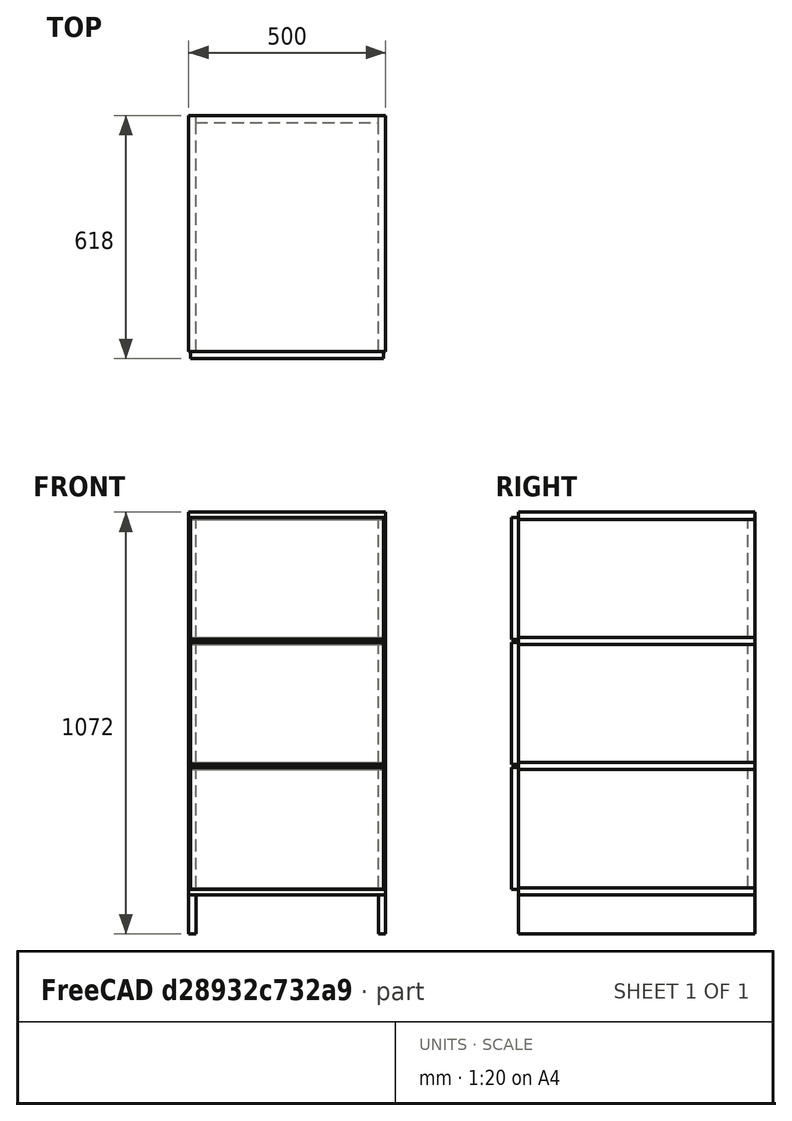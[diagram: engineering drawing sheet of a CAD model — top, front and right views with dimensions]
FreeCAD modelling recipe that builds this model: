
FCSTD DOCUMENT  (FreeCAD 0.20R29177 (Git))
Label: Demo009_approximation
License: All rights reserved
LicenseURL: http://en.wikipedia.org/wiki/All_rights_reserved
objects: Part::Box×18, App::DocumentObjectGroup×10, Spreadsheet::Sheet×1, TechDraw::DrawSVGTemplate×1, TechDraw::DrawViewSpreadsheet×1, TechDraw::DrawPage×1
note: 18 computed .brp shape members not serialized (recipe doc carries the construction recipe); baked Part::Feature solids carry a one-line shape summary decoded from their .brp

FEATURE [Part::Box] Box006  label="Foot L"
  AttacherType = Attacher::AttachEngine3D
  Height = 100
  Length = 18
  Width = 600
FEATURE [Part::Box] Box007  label="Side L1"
  AttacherType = Attacher::AttachEngine3D
  Height = 300
  Length = 18
  Placement = pos=(0,0,118) rot=(0,0,1;0rad)
  Width = 600
FEATURE [Part::Box] Box008  label="Side L2"
  AttacherType = Attacher::AttachEngine3D
  Height = 300
  Length = 18
  Placement = pos=(0,0,436) rot=(0,0,1;0rad)
  Width = 600
FEATURE [Part::Box] Box009  label="Side L3"
  AttacherType = Attacher::AttachEngine3D
  Height = 300
  Length = 18
  Placement = pos=(0,0,754) rot=(0,0,1;0rad)
  Width = 600
FEATURE [Part::Box] Box010  label="Foot R"
  AttacherType = Attacher::AttachEngine3D
  Height = 100
  Length = 18
  Placement = pos=(482,0,0) rot=(0,0,1;0rad)
  Width = 600
FEATURE [Part::Box] Box011  label="Side R1"
  AttacherType = Attacher::AttachEngine3D
  Height = 300
  Length = 18
  Placement = pos=(482,0,118) rot=(0,0,1;0rad)
  Width = 600
FEATURE [Part::Box] Box012  label="Side R2"
  AttacherType = Attacher::AttachEngine3D
  Height = 300
  Length = 18
  Placement = pos=(482,0,436) rot=(0,0,1;0rad)
  Width = 600
FEATURE [Part::Box] Box013  label="Side R3"
  AttacherType = Attacher::AttachEngine3D
  Height = 300
  Length = 18
  Placement = pos=(482,0,754) rot=(0,0,1;0rad)
  Width = 600
FEATURE [Part::Box] Box018  label="Back 1"
  AttacherType = Attacher::AttachEngine3D
  Height = 300
  Length = 464
  Placement = pos=(18,582,118) rot=(0,0,1;0rad)
  Width = 18
FEATURE [Part::Box] Box019  label="Back 2"
  AttacherType = Attacher::AttachEngine3D
  Height = 300
  Length = 464
  Placement = pos=(18,582,436) rot=(0,0,1;0rad)
  Width = 18
FEATURE [Part::Box] Box020  label="Back 3"
  AttacherType = Attacher::AttachEngine3D
  Height = 300
  Length = 464
  Placement = pos=(18,582,754) rot=(0,0,1;0rad)
  Width = 18
FEATURE [Part::Box] Box023  label="Top 1"
  AttacherType = Attacher::AttachEngine3D
  Height = 18
  Length = 500
  Placement = pos=(0,0,100) rot=(0,0,1;0rad)
  Width = 600
FEATURE [Part::Box] Box024  label="Top 2"
  AttacherType = Attacher::AttachEngine3D
  Height = 18
  Length = 500
  Placement = pos=(0,0,418) rot=(0,0,1;0rad)
  Width = 600
FEATURE [Part::Box] Box025  label="Top 3"
  AttacherType = Attacher::AttachEngine3D
  Height = 18
  Length = 500
  Placement = pos=(0,0,736) rot=(0,0,1;0rad)
  Width = 600
FEATURE [Part::Box] Box026  label="Top 4"
  AttacherType = Attacher::AttachEngine3D
  Height = 18
  Length = 500
  Placement = pos=(0,0,1054) rot=(0,0,1;0rad)
  Width = 600
FEATURE [Part::Box] Box027  label="Front 1"
  AttacherType = Attacher::AttachEngine3D
  Height = 310
  Length = 490
  Placement = pos=(5,-18,113) rot=(0,0,1;0rad)
  Width = 18
FEATURE [Part::Box] Box028  label="Front 2"
  AttacherType = Attacher::AttachEngine3D
  Height = 310
  Length = 490
  Placement = pos=(5,-18,431) rot=(0,0,1;0rad)
  Width = 18
FEATURE [Part::Box] Box029  label="Front 3"
  AttacherType = Attacher::AttachEngine3D
  Height = 310
  Length = 490
  Placement = pos=(5,-18,749) rot=(0,0,1;0rad)
  Width = 18
FEATURE [App::DocumentObjectGroup] Group006  label="Front"
  Group = -> [Box027,Box028,Box029]
FEATURE [App::DocumentObjectGroup] Group005  label="Top"
  Group = -> [Box023,Box024,Box025,Box026]
FEATURE [App::DocumentObjectGroup] Group004  label="Back"
  Group = -> [Box018,Box019,Box020]
FEATURE [App::DocumentObjectGroup] Group003  label="Side"
  Group = -> [Box007,Box008,Box009,Box011,Box012,Box013]
FEATURE [App::DocumentObjectGroup] Group007  label="Foot"
  Group = -> [Box006,Box010]
FEATURE [App::DocumentObjectGroup] Group  label="Back, no grain"
  Group = -> [Group004]
FEATURE [App::DocumentObjectGroup] Group009  label="Top, grain vertical"
  Group = -> [Group005]
FEATURE [App::DocumentObjectGroup] Group010  label="Foot, grain horizontal"
  Group = -> [Group007]
FEATURE [App::DocumentObjectGroup] Group011  label="Front, grain horizontal"
  Group = -> [Group006]
FEATURE [App::DocumentObjectGroup] Group012  label="Side, grain horizontal"
  Group = -> [Group003]
FEATURE [Spreadsheet::Sheet] toCut
  cells = A1=Length; B1=Width; C1=Qty; D1=Material; E1=Label; F1=Enabled; G1=Grain direction; H1=Top band; I1=Left band; J1=Bottom band; K1=Right band; A2=100; B2=600; C2=2; D2=18; E2=Foot; F2=true; G2=h; A3=300; B3=600; C3=6; D3=18; E3=Side; F3=true; G3=h; A4=300; B4=464; C4=3; D4=18; E4=Back; F4=true; A5=500; B5=600; C5=4; D5=18; E5=Top; F5=true; G5=v; A6=310; B6=490; C6=3; D6=18; E6=Front; F6=true; G6=h
FEATURE [TechDraw::DrawSVGTemplate] Template
  Height = 210
  Orientation = 1
  Width = 297
FEATURE [TechDraw::DrawViewSpreadsheet] Sheet
  CellEnd = K8
  CellStart = A1
  Font = DejaVu Sans
  LineWidth = 0.1
  LockPosition = false
  Rotation = 0
  ScaleType = 2
  Source = -> toCut
  Symbol = <blob: 19247 chars omitted>
  TextSize = 13
  X = 148
  Y = 105
FEATURE [TechDraw::DrawPage] toPrint
  KeepUpdated = true
  NextBalloonIndex = 1
  ProjectionType = 0
  Template = -> Template
  Views = -> [Sheet]
